# Revit family: Differential Pressure Control Valve 4002 FIX TS 23kPa
name_source: partatom
category: Rohrzubehör
revit_build: Autodesk Revit 2018 (Build: 20190510_1515(x64)
units: mm (PartAtom-declared; Revit-internal decimal feet)

## family parameters
Arbeitsebenenbasiert = Nein
Beim Laden mit Abzugskörper schneiden = Nein
Bemaßung runder Anschluss = Durchmesser verwenden
Gemeinsam genutzt = Nein
Immer vertikal = Ja
OmniClass-Nummer = 23.65.55.14
OmniClass-Titel = Valves for Liquid Services
Teiletyp = Unterbricht

## types (2) — shared parameters
Application = Differential pressure controllers are used to stabilize the differential pressure in heating and cooling circuits and ensure the
independence of the loads from dynamic pressure fluctuations in the system.
B01 = 10 mm  [stored 0.0328084 ft]
B02 = 104.688 mm
B03 = 44.5 mm  [stored 0.145997 ft]
B04 = 100.649 mm
Body = DZR brass CC770S
Compression spring = spring steel, rust and acid persistent
Connection nipple = brass CW602N
Connection thread for the drive = brass CW602N
Control range = FIX 23kPa
H03 = 9.8 mm
H04 = 4 mm  [stored 0.0131234 ft]
Hersteller = HERZ-Armaturen Ges.m.b.H
Insulation shell = EPP (expanded polypropylen)
J1 = 6.5 mm
J10 = 18.897 mm
J11 = 3.5 mm  [stored 0.0114829 ft]
J2 = 11 mm  [stored 0.0360892 ft]
J3 = 3.2 mm
J4 = 1.5 mm  [stored 0.00492126 ft]
J5 = 6.5 mm
J6 = 3.9 mm
J7 = 15.897 mm
J8 = 7.85 mm
J9 = 15.7 mm
K1 = 6.651 mm
K1.1 = 2.35 mm
K10 = 18.25 mm  [stored 0.0598753 ft]
K11 = 35 mm  [stored 0.114829 ft]
K12 = 10 mm  [stored 0.0328084 ft]
K13 = 16.649 mm
K14 = 16.649 mm
K15 = 26.649 mm
K16 = 3 mm  [stored 0.00984252 ft]
K17 = 66.7 mm
K18 = 89 mm  [stored 0.291995 ft]
K2 = 2.35 mm
K3 = 15 mm
K4 = 12 mm  [stored 0.0393701 ft]
K5 = 13 mm
K6 = 11.7 mm
K7 = 8.7 mm
K8 = 55 mm
K9 = 4 mm  [stored 0.0131234 ft]
L06 = 7 mm  [stored 0.0229659 ft]
Max. differential pressure on the body = 400000.0 Pa
Max. operating pressure = 1600000.0 Pa
Max. operating temperature from DN40 = 110 °C
Max. operating temperature up to DN32 = 130 °C
Membrane = EPDM
Membrane body = brass CW602N
Min. operating temperature (anti freeze) = -20 °C
Min. operating temperature (pure water) = 2 °C
O-Rings = EPDM
R02 = 14.5 mm
Regulator connection nut = brass CW614N
S07 = 10 mm  [stored 0.0328084 ft]
SCRNCODE = 05;03;4
SCRNSEQ = ARM;ARM_TYP="DIFR";2
URL = www.herzvalves.com
V10 = 16 mm  [stored 0.0524934 ft]
V12 = 17 mm
Valve shaft = stainless steel 14301
k19 = 2 mm  [stored 0.00656168 ft]
k20 = 14 mm  [stored 0.0459318 ft]
k21 = 13 mm
k22 = 22 mm
k23 = 6 mm  [stored 0.019685 ft]
k24 = 13 mm
k25 = 9 mm  [stored 0.0295276 ft]

## per-type parameters (varying)
| type | Dämmung | Materials | Medium | Model |
| with insulation | Ja | Ammonia contained in hemp can damage brass valve bodies, EPDM gaskets can be affected by
Mineral oils lubricants and thus lead to failure of the EPDM seals. Please refer to manufacturers
documentation when using ethylene glycol products for frost and corrosion protection. | Water purity in accordance with the ÖNORM H 5195 and VDI 2035 standards
Ethylene and propylene glycol can be mixed to a ratio of 25 - 50 vol. [%] | The differential pressure controller is a straight-version linear controller and works without auxiliary
power. The fixed nominal differential pressure is 23 kPa.
A capillary (1000 mm) is included and should be connected to the circuit regulating valve in the
flow. |
| without insulation | Nein | Ammonia contained in hemp can damage brass valve bodies, EPDM gaskets can be affected by
mineral oil lubricants and thus lead to failure of the EPDM seals. Please refer to manufacturers
documentation when using ethylene glycol products for frost and corrosion protection. | Water purity in accordance with the ÖNORM H 5195 and VDI 2035 standards.
Ethylene and propylene glycol can be mixed to a ratio of 25 - 50 vol. [%] | The differential pressure controller is a straight-version linear controller and works without auxiliary
power. The fixed nominal differential pressure is 23 kPa.
A capillary (1000 mm) is included and should be connected to the circuit regulating valve in the supply line. |

note: [stored X ft] marks values corroborated as IEEE doubles in the binary element streams (Revit-internal decimal feet)
